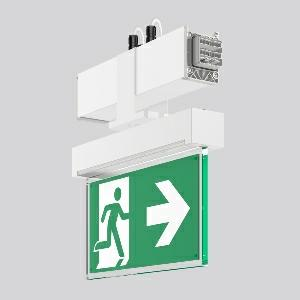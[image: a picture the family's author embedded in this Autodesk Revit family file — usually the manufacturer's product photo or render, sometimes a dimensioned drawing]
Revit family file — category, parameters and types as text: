
# Revit family: linedo_module_rz_9503rz_762_430_030_6cd0
name_source: partatom
category: Lighting Fixtures
units: mm (PartAtom-declared; Revit-internal decimal feet)

## family parameters
Cut with Voids When Loaded = No
Host = Face
Light Source = No
Part Type = Normal
Room Calculation Point = No
Round Connector Dimension = Use Diameter
Shared = No

## types (1)
- LINEDO Module RZ
    Apparent Load = 0 VA
    Default Elevation = 1800 mm
    Description = LINEDO, white, on/off
Continuous line luminaire, L 336 B 62 H 343, SBS, 3 h, automatischer Selbsttest
    Height = 343 mm
    Lamp = 0 x
    Length = 336 mm
    Luminous efficacy = 0 lm/W
    Manufacturer = RZB
    ModVariant = No
    Model = 9503RZ.762.430.030
    Mounting Place = Ceiling
    Mounting Type = Surface mounted
    Number of Poles = 1
    OnlyDefault = Yes
    Power Factor = 1
    Product Name = LINEDO Module RZ
    Product group = Continuous line luminaire system Linedo IP 54
    ProductGroupID = 314
    Protection Class = Protection class I
    Protection Degree = IP 54
    RLX_Detail_Level = 1
    RLX_Emergency_Light_Flux = 0 lm
    RLX_Emergency_Type = 0
    RLX_Emergency_Type_DB = No
    RlxData = <blob elided: 35689 chars, md5=cae82797>
    Standby Power = 0 W
    System Light Flux = 0 lm
    System Power = 0 W
    Type Comments = Product without accessories
    Type Image = 9503rz.762.434.030.jpg
    URL = http://relux.com
    VarID = ---
    Voltage = 0 V
    Weight = 0.00 kg
    Width = 62 mm  [stored 0.203412 ft]

note: [stored X ft] marks values corroborated as IEEE doubles in the binary element streams (Revit-internal decimal feet)

## geometry (parser evidence)
native form markers: Blend x4, Sweep x10
no freeform markers — native parametric forms only
